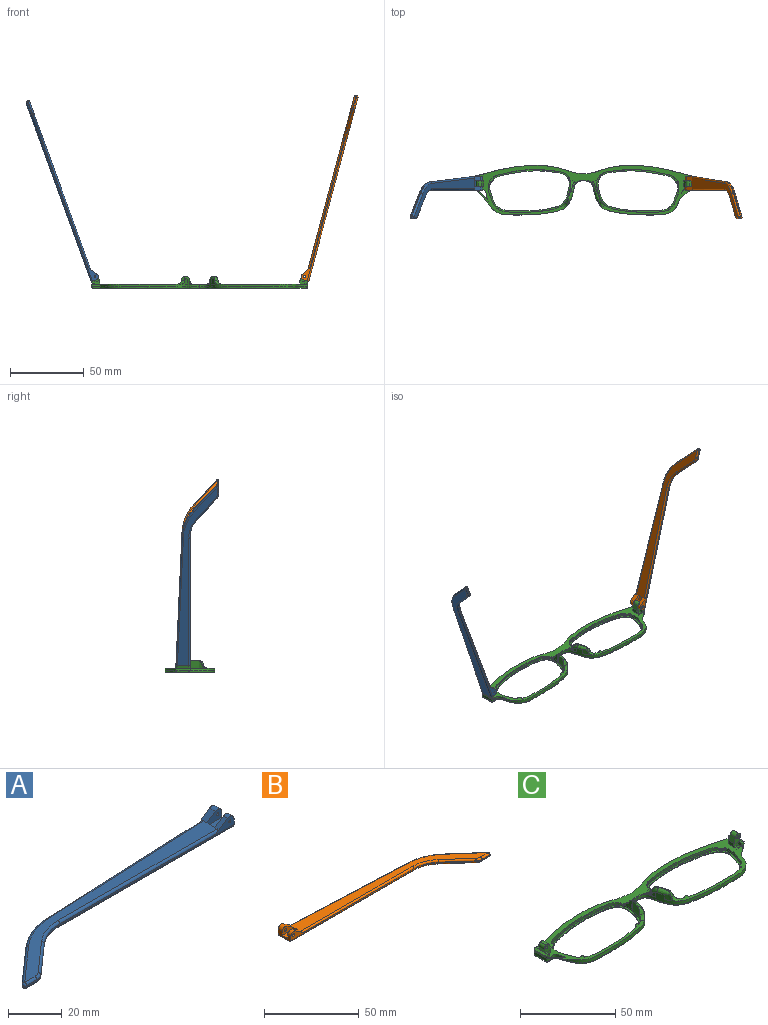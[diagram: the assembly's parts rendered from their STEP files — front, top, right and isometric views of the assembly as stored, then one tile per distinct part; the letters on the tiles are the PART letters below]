
ASSEMBLY  parts=3 mates=2
PART A: 43 faces, bbox 130.2x29.5x5.9 mm
  f0: plane 9.62x3.72mm, normal (1,0,0), area 24.7mm2, adj f1,f3,f4,f5,f10,f16,f18,f28
  f1: cylinder r=2.2mm len=3.45mm, axis (0,-1,0), area 11mm2, adj f0,f2,f4,f37
  f2: plane 6.01x3.91mm, normal (-0.55,0,0.84), area 12.7mm2, adj f1,f4,f9,f19,f37
  f3: plane 2.26x0.1mm, normal (0,0,1), area 0.1mm2, adj f0,f5,f18
  f4: plane 92.1x4.9mm, normal (0,-1,0), area 79.9mm2, adj f0,f1,f2,f14,f19,f36,f42
  f5: plane 93.42x4.13mm, normal (-0.04,1,0), area 64.8mm2, adj f0,f3,f11,f15,f17,f27,f28
  f6: plane 17.82x15.72mm, normal (-0.66,0.75,0), area 14.3mm2, adj f11,f12,f25,f30
  f7: plane 5.46x0.6mm, normal (0,-1,0), area 3.3mm2, adj f12,f13,f23,f32
  f8: plane 14.99x13.23mm, normal (0.66,-0.75,0), area 12mm2, adj f13,f14,f21,f34
  f9: plane 121.18x26.73mm, normal (0,0,1), area 627.7mm2, adj f2,f17,f19,f20,f21,f22,f23,f25
  f10: plane 129.1x27.08mm, normal (0,0,-1), area 686.5mm2, adj f0,f28,f29,f30,f32,f33,f34,f35
  f11: cylinder r=30mm len=18.52mm, axis (0,0,-1), area 12.2mm2, adj f5,f6,f26,f29
  f12: cylinder r=1mm len=1.75mm, axis (0,0,-1), area 1.5mm2, adj f6,f7,f24,f31
  f13: cylinder r=5mm len=3.31mm, axis (0,0,-1), area 2.2mm2, adj f7,f8,f22,f33
  f14: cylinder r=20mm len=13.23mm, axis (0,0,1), area 8.7mm2, adj f4,f8,f20,f35
  f15: plane 5.66x0.25mm, normal (0,0,-1), area 0.7mm2, adj f5,f17,f18
  f16: cylinder r=2.2mm len=3.45mm, axis (0,-1,0), area 14.8mm2, adj f0,f17,f18,f38
  f17: plane 6.01x3.91mm, normal (-0.55,0,0.84), area 16.9mm2, adj f5,f9,f15,f16,f18,f27,f38
  f18: plane 7.92x3.3mm, normal (0,1,0), area 15.9mm2, adj f0,f3,f15,f16,f17,f41
  f19: cylinder r=1mm len=84.18mm, axis (-1,0,0), area 131.4mm2, adj f2,f4,f9,f20
  f20: torus R=21mm, axis (0,0,1), area 23.1mm2, adj f9,f14,f19,f21
  f21: cylinder r=1mm len=15.65mm, axis (-0.75,-0.66,0), area 31.4mm2, adj f8,f9,f20,f22
  f22: torus R=4mm, axis (0,0,1), area 5.3mm2, adj f9,f13,f21,f23
  f23: cylinder r=1mm len=5.46mm, axis (-1,0,0), area 8.6mm2, adj f7,f9,f22,f24
  f24: sphere r=1mm, area 2.4mm2, adj f12,f23,f25
  f25: cylinder r=1mm len=18.48mm, axis (0.75,0.66,0), area 37.3mm2, adj f6,f9,f24,f26
  f26: torus R=29mm, axis (0,0,1), area 31.6mm2, adj f9,f11,f25,f27
  f27: cylinder r=1mm len=85.5mm, axis (1,0.04,0), area 133.5mm2, adj f5,f9,f17,f26
  f28: cylinder r=1mm len=93.46mm, axis (-1,-0.04,0), area 146.9mm2, adj f0,f5,f10,f29
  f29: torus R=29mm, axis (0,0,1), area 31.6mm2, adj f10,f11,f28,f30
  f30: cylinder r=1mm len=18.48mm, axis (-0.75,-0.66,0), area 37.3mm2, adj f6,f10,f29,f31
  f31: sphere r=1mm, area 2.4mm2, adj f12,f30,f32
  f32: cylinder r=1mm len=5.46mm, axis (1,0,0), area 8.6mm2, adj f7,f10,f31,f33
  f33: torus R=4mm, axis (0,0,1), area 5.3mm2, adj f10,f13,f32,f34
  f34: cylinder r=1mm len=15.65mm, axis (0.75,0.66,0), area 31.4mm2, adj f8,f10,f33,f35
  f35: torus R=21mm, axis (0,0,1), area 23.1mm2, adj f10,f14,f34,f36
  f36: cylinder r=1mm len=92.1mm, axis (1,0,0), area 144.7mm2, adj f0,f4,f10,f35
  f37: plane 7.92x4.7mm, normal (0,1,0), area 27mm2, adj f0,f1,f2,f39,f40,f42
  f38: plane 7.92x4.7mm, normal (0,-1,0), area 27mm2, adj f0,f16,f17,f39,f40,f41
  f39: plane 7.92x4.1mm, normal (0,0,1), area 32.5mm2, adj f0,f37,f38,f40
  f40: plane 4.1x1.4mm, normal (1,0,0), area 5.7mm2, adj f9,f37,f38,f39
  f41: cylinder r=0.5mm len=3.1mm, axis (0,-1,0), area 9.7mm2, adj f18,f38
  f42: cylinder r=0.5mm len=2.3mm, axis (0,-1,0), area 7.2mm2, adj f4,f37
PART B: 43 faces, bbox 130.2x29.5x5.9 mm
  f0: plane 9.62x3.72mm, normal (-1,0,0), area 24.7mm2, adj f1,f3,f4,f5,f10,f16,f18,f28
  f1: cylinder r=2.2mm len=3.45mm, axis (0,-1,0), area 11mm2, adj f0,f2,f4,f37
  f2: plane 6.01x3.91mm, normal (0.55,0,0.84), area 12.7mm2, adj f1,f4,f9,f19,f37
  f3: plane 2.26x0.1mm, normal (0,0,1), area 0.1mm2, adj f0,f5,f18
  f4: plane 92.1x4.9mm, normal (0,-1,0), area 78.2mm2, adj f0,f1,f2,f14,f19,f36,f42
  f5: plane 93.42x4.13mm, normal (0.04,1,0), area 64.8mm2, adj f0,f3,f11,f15,f17,f27,f28
  f6: plane 17.82x15.72mm, normal (0.66,0.75,0), area 14.3mm2, adj f11,f12,f25,f30
  f7: plane 5.46x0.6mm, normal (0,-1,0), area 3.3mm2, adj f12,f13,f23,f32
  f8: plane 14.99x13.23mm, normal (-0.66,-0.75,0), area 12mm2, adj f13,f14,f21,f34
  f9: plane 121.18x26.73mm, normal (0,0,1), area 627.7mm2, adj f2,f17,f19,f20,f21,f22,f23,f25
  f10: plane 129.1x27.08mm, normal (0,0,-1), area 686.5mm2, adj f0,f28,f29,f30,f32,f33,f34,f35
  f11: cylinder r=30mm len=18.52mm, axis (0,0,-1), area 12.2mm2, adj f5,f6,f26,f29
  f12: cylinder r=1mm len=1.75mm, axis (0,0,-1), area 1.5mm2, adj f6,f7,f24,f31
  f13: cylinder r=5mm len=3.31mm, axis (0,0,-1), area 2.2mm2, adj f7,f8,f22,f33
  f14: cylinder r=20mm len=13.23mm, axis (0,0,1), area 8.7mm2, adj f4,f8,f20,f35
  f15: plane 5.66x0.25mm, normal (0,0,-1), area 0.7mm2, adj f5,f17,f18
  f16: cylinder r=2.2mm len=3.45mm, axis (0,-1,0), area 14.8mm2, adj f0,f17,f18,f38
  f17: plane 6.01x3.91mm, normal (0.55,0,0.84), area 16.9mm2, adj f5,f9,f15,f16,f18,f27,f38
  f18: plane 7.92x3.3mm, normal (0,1,0), area 14.3mm2, adj f0,f3,f15,f16,f17,f41
  f19: cylinder r=1mm len=84.18mm, axis (1,0,0), area 131.4mm2, adj f2,f4,f9,f20
  f20: torus R=21mm, axis (0,0,1), area 23.1mm2, adj f9,f14,f19,f21
  f21: cylinder r=1mm len=15.65mm, axis (0.75,-0.66,0), area 31.4mm2, adj f8,f9,f20,f22
  f22: torus R=4mm, axis (0,0,1), area 5.3mm2, adj f9,f13,f21,f23
  f23: cylinder r=1mm len=5.46mm, axis (1,0,0), area 8.6mm2, adj f7,f9,f22,f24
  f24: sphere r=1mm, area 2.4mm2, adj f12,f23,f25
  f25: cylinder r=1mm len=18.48mm, axis (-0.75,0.66,0), area 37.3mm2, adj f6,f9,f24,f26
  f26: torus R=29mm, axis (0,0,1), area 31.6mm2, adj f9,f11,f25,f27
  f27: cylinder r=1mm len=85.5mm, axis (-1,0.04,0), area 133.5mm2, adj f5,f9,f17,f26
  f28: cylinder r=1mm len=93.46mm, axis (1,-0.04,0), area 146.9mm2, adj f0,f5,f10,f29
  f29: torus R=29mm, axis (0,0,1), area 31.6mm2, adj f10,f11,f28,f30
  f30: cylinder r=1mm len=18.48mm, axis (0.75,-0.66,0), area 37.3mm2, adj f6,f10,f29,f31
  f31: sphere r=1mm, area 2.4mm2, adj f12,f30,f32
  f32: cylinder r=1mm len=5.46mm, axis (-1,0,0), area 8.6mm2, adj f7,f10,f31,f33
  f33: torus R=4mm, axis (0,0,1), area 5.3mm2, adj f10,f13,f32,f34
  f34: cylinder r=1mm len=15.65mm, axis (-0.75,0.66,0), area 31.4mm2, adj f8,f10,f33,f35
  f35: torus R=21mm, axis (0,0,1), area 23.1mm2, adj f10,f14,f34,f36
  f36: cylinder r=1mm len=92.1mm, axis (-1,0,0), area 144.7mm2, adj f0,f4,f10,f35
  f37: plane 7.92x4.7mm, normal (0,1,0), area 25.4mm2, adj f0,f1,f2,f39,f40,f42
  f38: plane 7.92x4.7mm, normal (0,-1,0), area 25.4mm2, adj f0,f16,f17,f39,f40,f41
  f39: plane 7.92x4.1mm, normal (0,0,1), area 32.5mm2, adj f0,f37,f38,f40
  f40: plane 4.1x1.4mm, normal (-1,0,0), area 5.7mm2, adj f9,f37,f38,f39
  f41: cylinder r=0.88mm len=3.1mm, axis (0,-1,0), area 17mm2, adj f18,f38
  f42: cylinder r=0.88mm len=2.3mm, axis (0,-1,0), area 12.6mm2, adj f4,f37
PART C: 120 faces, bbox 148.2x34.9x18 mm
  f0: bspline ~1.76x1.18mm, area 0.5mm2, adj f2,f8,f38,f53
  f1: plane 147.39x34.08mm, normal (0,0,1), area 837.7mm2, adj f6,f7,f8,f9,f13,f21,f24,f25
  f2: bspline ~6.08x4.89mm, area 11.7mm2, adj f0,f8,f38,f42,f44,f53,f54
  f3: plane 1.73x0.37mm, normal (0,0,1), area 0mm2, adj f13,f40
  f4: plane 3.67x1.77mm, normal (0,0,1), area 0.3mm2, adj f8,f39
  f5: plane 1.13x0.03mm, normal (0,0,1), area 0mm2, adj f8,f23
  f6: plane 6.97x5.07mm, normal (0,1,0), area 22.7mm2, adj f1,f21,f22,f26,f28,f29,f31,f32
  f7: plane 3.2x2.36mm, normal (0,-1,0), area 5.7mm2, adj f1,f21,f27,f30
  f8: extruded ~73.33x33.74mm, area 292.5mm2, adj f0,f1,f2,f4,f5,f9,f14,f15
  f9: extruded ~35.39x5.69mm, area 72.2mm2, adj f1,f8,f19,f69
  f10: plane 144.78x31.74mm, normal (0,0,-1), area 624.4mm2, adj f14,f16,f18,f19,f20,f73,f75,f77
  f11: plane 56.06x29.13mm, normal (0,0,1), area 134.7mm2, adj f12,f20
  f12: extruded ~55.47x28.99mm, area 149.6mm2, adj f11,f13
  f13: extruded ~55.47x28.99mm, area 198mm2, adj f1,f3,f12,f40,f41,f42,f43,f45
  f14: bspline ~73.03x24.27mm, area 148.1mm2, adj f8,f10,f15,f73
  f15: bspline ~1x1mm, area 0.8mm2, adj f8,f14,f16
  f16: bspline ~9.01x1.24mm, area 12.6mm2, adj f8,f10,f15,f17
  f17: bspline ~1.04x1mm, area 0.7mm2, adj f8,f16,f18
  f18: bspline ~45.74x8.55mm, area 59.8mm2, adj f8,f10,f17,f19
  f19: bspline ~38.59x6.7mm, area 56.6mm2, adj f9,f10,f18,f78
  f20: bspline ~56.14x29.15mm, area 219.1mm2, adj f10,f11
  f21: plane 4x2.36mm, normal (-1,0,0), area 9.5mm2, adj f1,f6,f7,f22
  f22: plane 4x0.02mm, normal (0.34,0,0.94), area 0.1mm2, adj f6,f21,f29
  f23: plane 2.85x2.63mm, normal (0,-1,0), area 3.9mm2, adj f5,f27,f28,f36,f57
  f24: plane 7.67x1.6mm, normal (0.94,0,-0.34), area 13mm2, adj f1,f36,f37,f57
  f25: plane 2.1x1.69mm, normal (0,1,0), area 2.8mm2, adj f1,f26,f28,f37,f57
  f26: plane 3.3x2.1mm, normal (-1,0,0), area 6.9mm2, adj f1,f6,f25,f28
  f27: plane 2.37x2.1mm, normal (-1,0,0), area 5mm2, adj f1,f7,f23,f28,f30
  f28: plane 9.67x1.24mm, normal (0,0,1), area 8.2mm2, adj f6,f23,f25,f26,f27,f30,f31,f57
  f29: plane 4x3.31mm, normal (-0.94,0,0.34), area 14.1mm2, adj f6,f22,f30,f33
  f30: plane 5.77x5.06mm, normal (0,-1,0), area 17mm2, adj f7,f27,f28,f29,f31,f32,f33,f34
  f31: plane 4x2.21mm, normal (0.94,0,-0.34), area 9.4mm2, adj f6,f28,f30,f34
  f32: plane 4x0.01mm, normal (0.34,0,0.94), area 0mm2, adj f6,f30,f33,f34
  f33: cylinder r=1.98mm len=4mm, axis (0,1,0), area 12.4mm2, adj f6,f29,f30,f32
  f34: cylinder r=1.98mm len=4mm, axis (0,-1,0), area 12.4mm2, adj f6,f30,f31,f32
  f35: cylinder r=0.88mm len=4mm, axis (0,-1,0), area 22mm2, adj f6,f30
  f36: cone r=1mm half-angle=20deg, axis (0,0,1), area 2.4mm2, adj f1,f23,f24,f57
  f37: cylinder r=1mm len=2.28mm, axis (-0.34,0,-0.94), area 3mm2, adj f1,f24,f25,f57
  f38: extruded ~3.67x3.15mm, area 6.1mm2, adj f0,f2,f8,f60
  f39: extruded ~3.67x3.59mm, area 13.9mm2, adj f4,f8,f43,f44,f56
  f40: extruded ~5x1.71mm, area 8.3mm2, adj f3,f13,f42
  f41: plane 5.07x1.76mm, normal (0,0,1), area 2.4mm2, adj f13,f42,f43,f44
  f42: bspline ~15.51x15.35mm, area 6.7mm2, adj f2,f13,f40,f41,f55
  f43: bspline ~6.43x5.06mm, area 8.8mm2, adj f13,f39,f41,f44,f56
  f44: bspline ~9.39x4.96mm, area 20mm2, adj f2,f8,f39,f41,f43
  f45: plane 3.19x1.36mm, normal (0,0,-1), area 2.1mm2, adj f13,f46
  f46: cylinder r=2.28mm len=3.16mm, axis (0,0,1), area 2.1mm2, adj f1,f13,f45,f55
  f47: plane 3.14x2.8mm, normal (0,0,-1), area 3.9mm2, adj f13,f48
  f48: cylinder r=2.28mm len=3.13mm, axis (0,0,1), area 2.5mm2, adj f1,f13,f47
  f49: plane 2.52x1.67mm, normal (0,0,-1), area 2.6mm2, adj f13,f50
  f50: cylinder r=1.3mm len=2.52mm, axis (0,0,1), area 2mm2, adj f1,f13,f49
  f51: plane 2.26x2.15mm, normal (0,0,-1), area 2.7mm2, adj f13,f52
  f52: cylinder r=1.3mm len=2.25mm, axis (0,0,1), area 2mm2, adj f1,f13,f51
  f53: bspline ~2.68x2.04mm, area 2mm2, adj f0,f2,f8,f54,f59
  f54: bspline ~3.55x3.47mm, area 3.7mm2, adj f1,f2,f53,f55,f59
  f55: bspline ~6.06x4.4mm, area 7.8mm2, adj f1,f13,f42,f46,f54
  f56: bspline ~5.98x4.28mm, area 10.1mm2, adj f1,f8,f13,f39,f43
  f57: plane 9.73x1.44mm, normal (0.34,0,0.94), area 13.9mm2, adj f23,f24,f25,f28,f36,f37
  f58: bspline ~6.26x2.27mm, area 2.6mm2, adj f1,f8,f59,f117
  f59: bspline ~2.07x1.47mm, area 0.6mm2, adj f8,f53,f54,f58
  f60: bspline ~5.11x1.64mm, area 0mm2, adj f8,f38
  f61: bspline ~2.15x1.37mm, area 0.5mm2, adj f62,f68,f97,f112
  f62: bspline ~6.08x4.89mm, area 11.7mm2, adj f61,f68,f97,f101,f103,f112,f113
  f63: plane 1.73x0.37mm, normal (0,0,1), area 0mm2, adj f72,f99
  f64: plane 3.67x1.77mm, normal (0,0,1), area 0.3mm2, adj f68,f98
  f65: plane 1.13x0.03mm, normal (0,0,1), area 0mm2, adj f68,f82
  f66: plane 6.97x5.07mm, normal (0,1,0), area 22.7mm2, adj f1,f80,f81,f85,f87,f88,f90,f91
  f67: plane 3.2x2.36mm, normal (0,-1,0), area 5.7mm2, adj f1,f80,f86,f89
  f68: extruded ~73.33x33.74mm, area 292.5mm2, adj f1,f8,f61,f62,f64,f65,f69,f73
  f69: extruded ~35.39x5.69mm, area 72.2mm2, adj f1,f9,f68,f78
  f70: plane 56.06x29.13mm, normal (0,0,1), area 134.7mm2, adj f71,f79
  f71: extruded ~55.47x28.99mm, area 149.6mm2, adj f70,f72
  f72: extruded ~55.47x28.99mm, area 198.5mm2, adj f1,f63,f71,f99,f100,f101,f102,f104
  f73: bspline ~73.03x24.27mm, area 148.1mm2, adj f10,f14,f68,f74
  f74: bspline ~1x1mm, area 0.8mm2, adj f68,f73,f75
  f75: bspline ~9.01x1.24mm, area 12.6mm2, adj f10,f68,f74,f76
  f76: bspline ~1.04x1mm, area 0.8mm2, adj f68,f75,f77
  f77: bspline ~45.74x8.55mm, area 59.8mm2, adj f10,f68,f76,f78
  f78: bspline ~38.59x6.7mm, area 56.6mm2, adj f10,f19,f69,f77
  f79: bspline ~56.14x29.15mm, area 219.1mm2, adj f10,f70
  f80: plane 4x2.36mm, normal (1,0,0), area 9.5mm2, adj f1,f66,f67,f81
  f81: plane 4x0.02mm, normal (-0.34,0,0.94), area 0.1mm2, adj f66,f80,f88
  f82: plane 2.85x2.63mm, normal (0,-1,0), area 3.9mm2, adj f65,f86,f87,f95,f116
  f83: plane 7.67x1.6mm, normal (-0.94,0,-0.34), area 13mm2, adj f1,f95,f96,f116
  f84: plane 2.1x1.69mm, normal (0,1,0), area 2.8mm2, adj f1,f85,f87,f96,f116
  f85: plane 3.3x2.1mm, normal (1,0,0), area 6.9mm2, adj f1,f66,f84,f87
  f86: plane 2.37x2.1mm, normal (1,0,0), area 5mm2, adj f1,f67,f82,f87,f89
  f87: plane 9.67x1.24mm, normal (0,0,1), area 8.2mm2, adj f66,f82,f84,f85,f86,f89,f90,f116
  f88: plane 4x3.31mm, normal (0.94,0,0.34), area 14.1mm2, adj f66,f81,f89,f92
  f89: plane 5.77x5.06mm, normal (0,-1,0), area 17mm2, adj f67,f86,f87,f88,f90,f91,f92,f93
  f90: plane 4x2.21mm, normal (-0.94,0,-0.34), area 9.4mm2, adj f66,f87,f89,f93
  f91: plane 4x0.01mm, normal (-0.34,0,0.94), area 0mm2, adj f66,f89,f92,f93
  f92: cylinder r=1.98mm len=4mm, axis (0,1,0), area 12.4mm2, adj f66,f88,f89,f91
  f93: cylinder r=1.98mm len=4mm, axis (0,-1,0), area 12.4mm2, adj f66,f89,f90,f91
  f94: cylinder r=0.88mm len=4mm, axis (0,-1,0), area 22mm2, adj f66,f89
  f95: cone r=1mm half-angle=20deg, axis (0,0,1), area 2.4mm2, adj f1,f82,f83,f116
  f96: cylinder r=1mm len=2.28mm, axis (0.34,0,-0.94), area 3mm2, adj f1,f83,f84,f116
  f97: extruded ~3.67x3.15mm, area 6.1mm2, adj f61,f62,f68,f119
  f98: extruded ~3.67x3.59mm, area 13.9mm2, adj f64,f68,f102,f103,f115
  f99: extruded ~5x1.71mm, area 8.3mm2, adj f63,f72,f101
  f100: plane 5.07x1.76mm, normal (0,0,1), area 2.4mm2, adj f72,f101,f102,f103
  f101: bspline ~15.51x15.35mm, area 6.7mm2, adj f62,f72,f99,f100,f114
  f102: bspline ~6.43x5.06mm, area 8.8mm2, adj f72,f98,f100,f103,f115
  f103: bspline ~9.39x4.96mm, area 20mm2, adj f62,f68,f98,f100,f102
  f104: plane 3.19x1.36mm, normal (0,0,-1), area 2.1mm2, adj f72,f105
  f105: cylinder r=2.28mm len=3.16mm, axis (0,0,1), area 2.1mm2, adj f1,f72,f104,f114
  f106: plane 3.14x2.8mm, normal (0,0,-1), area 3.9mm2, adj f72,f107
  f107: cylinder r=2.28mm len=3.13mm, axis (0,0,1), area 2.5mm2, adj f1,f72,f106
  f108: plane 2.52x1.67mm, normal (0,0,-1), area 2.6mm2, adj f72,f109
  f109: cylinder r=1.3mm len=2.52mm, axis (0,0,1), area 2mm2, adj f1,f72,f108
  f110: plane 2.26x2.15mm, normal (0,0,-1), area 2.7mm2, adj f72,f111
  f111: cylinder r=1.3mm len=2.25mm, axis (0,0,1), area 2mm2, adj f1,f72,f110
  f112: bspline ~2.67x2.03mm, area 2mm2, adj f61,f62,f68,f113,f118
  f113: bspline ~3.55x3.47mm, area 3.7mm2, adj f1,f62,f112,f114,f118
  f114: bspline ~5.84x4.37mm, area 7.8mm2, adj f1,f72,f101,f105,f113
  f115: bspline ~5.98x4.28mm, area 10.1mm2, adj f1,f68,f72,f98,f102
  f116: plane 9.73x1.44mm, normal (-0.34,0,0.94), area 13.9mm2, adj f82,f83,f84,f87,f95,f96
  f117: bspline ~6.26x2.27mm, area 2.6mm2, adj f1,f58,f68,f118
  f118: bspline ~2.07x1.47mm, area 0.6mm2, adj f68,f112,f113,f117
  f119: bspline ~5.11x1.64mm, area 0mm2, adj f68,f97
PLACE A rot(axis=(0,1,0),70deg) t=(-84.77,-5.75,56)mm
PLACE B rot(axis=(0,-1,0),75deg) t=(68.2,-5.75,-61.61)mm
PLACE C t=(10.15,-1.13,-5.77)mm
MATE revolute A.f1 <-> C.f92  axis (0,-1,0) through (-60.89,2.72,1.22)mm
MATE revolute B.f41 <-> C.f34  axis (0,-1,0) through (81.2,2.72,1.21)mm
